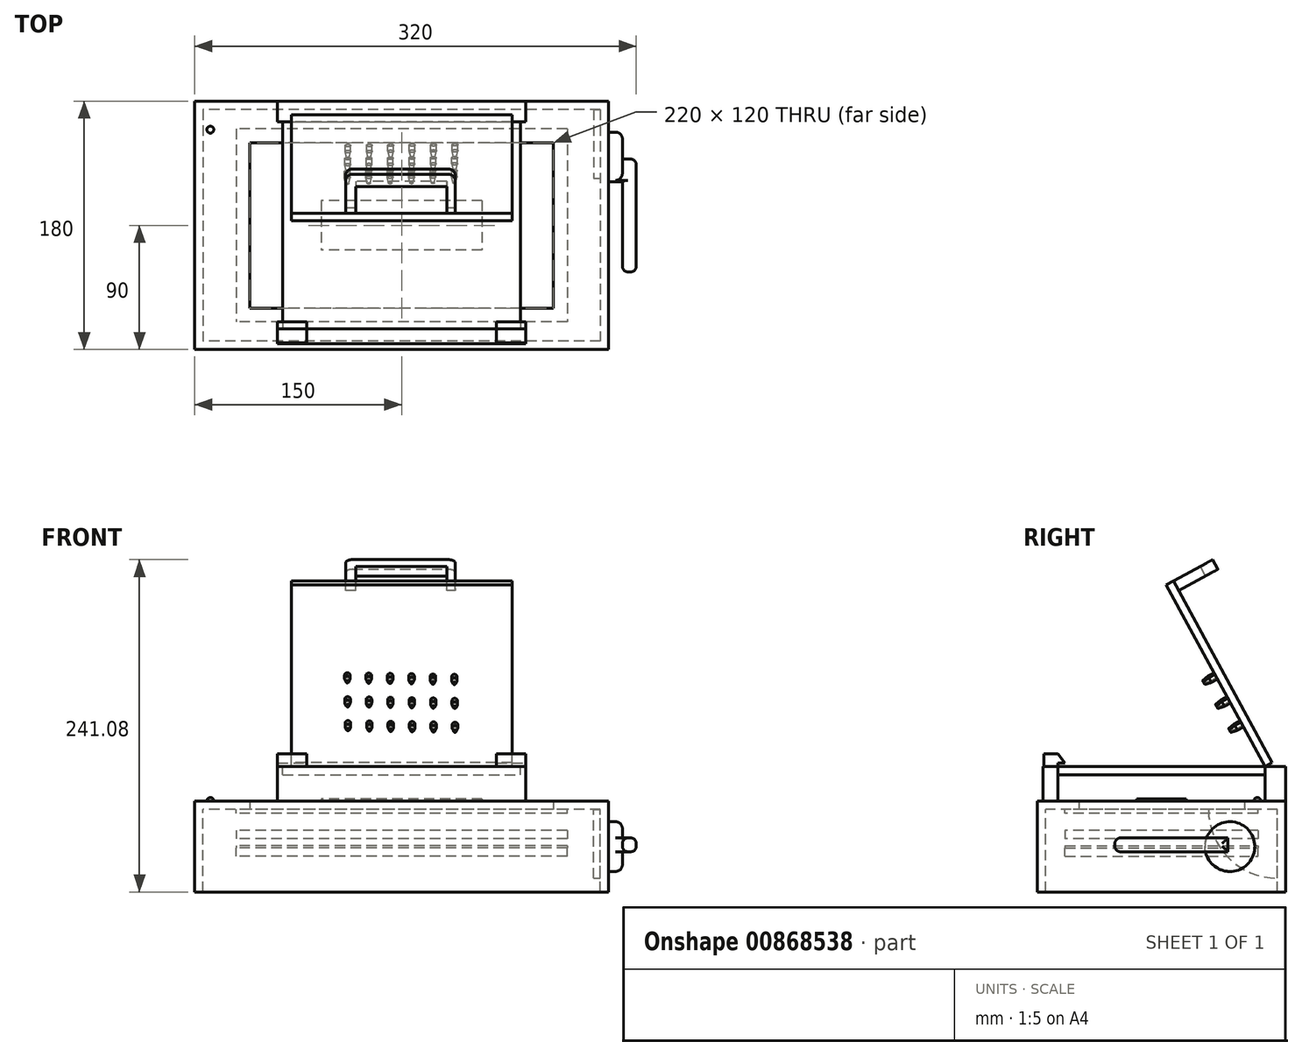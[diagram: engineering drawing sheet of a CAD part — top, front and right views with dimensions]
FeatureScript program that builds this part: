
annotation { "Feature Type Name" : "Feature", "Feature Type Description" : "" }
export const myFeature = defineFeature(function(context is Context, id is Id, definition is map)
    precondition{}
    {
        {
            var Q0;
            Q0=qCreatedBy(makeId("Top.planeOp"),FACE);
            var sketch = newSketch(context, id + "F0", { "sketchPlane" : qUnion([Q0])});
            skLineSegment(sketch, "E0.bottom", {"start": v(150, 90) * mm, "end": v(-150, 90) * mm});
            skLineSegment(sketch, "E0.top", {"start": v(150, -90) * mm, "end": v(-150, -90) * mm});
            skLineSegment(sketch, "E0.left", {"start": v(150, 90) * mm, "end": v(150, -90) * mm});
            skLineSegment(sketch, "E0.right", {"start": v(-150, 90) * mm, "end": v(-150, -90) * mm});
            skPoint(sketch, "E0.middle", {"position": v(0, 0) * mm});
            skLineSegment(sketch, "E1.bottom", {"start": v(110, 60) * mm, "end": v(-110, 60) * mm});
            skLineSegment(sketch, "E1.top", {"start": v(110, -60) * mm, "end": v(-110, -60) * mm});
            skLineSegment(sketch, "E1.left", {"start": v(110, 60) * mm, "end": v(110, -60) * mm});
            skLineSegment(sketch, "E1.right", {"start": v(-110, 60) * mm, "end": v(-110, -60) * mm});
            skSolve(sketch);
        }
        {
            var Q0;
            Q0 = qSketchRegion(id + "F0", true);
            extrude(context, id + "F1", {"entities" : qUnion([Q0]), "depth" : 6 * mm, "offsetDistance" : 25 * mm});
        }
        {
            var Q0;
            Q0=qCreatedBy(makeId("Top.planeOp"),FACE);
            var sketch = newSketch(context, id + "F2", { "sketchPlane" : qUnion([Q0])});
            skLineSegment(sketch, "E2.bottom", {"start": v(120, 70) * mm, "end": v(-120, 70) * mm});
            skLineSegment(sketch, "E2.top", {"start": v(120, -70) * mm, "end": v(-120, -70) * mm});
            skLineSegment(sketch, "E2.left", {"start": v(120, 70) * mm, "end": v(120, -70) * mm});
            skLineSegment(sketch, "E2.right", {"start": v(-120, 70) * mm, "end": v(-120, -70) * mm});
            skPoint(sketch, "E2.middle", {"position": v(0, 0) * mm});
            skSolve(sketch);
        }
        {
            var Q0;
            Q0 = qSketchRegion(id + "F2", true);
            extrude(context, id + "F3", {"entities" : qUnion([Q0]), "oppositeDirection" : true, "depth" : 3 * mm, "offsetDistance" : 25 * mm});
        }
        {
            var Q0;
            Q0=makeQuery(id+"F1.opExtrude","CAP_FACE",FACE,{"disambiguationData":[OSD([sQuery(id+"F0.wireOp",EDGE,"E0.bottom"),sQuery(id+"F0.wireOp",EDGE,"E0.top"),sQuery(id+"F0.wireOp",EDGE,"E0.left"),sQuery(id+"F0.wireOp",EDGE,"E0.right"),sQuery(id+"F0.wireOp",EDGE,"E1.bottom"),sQuery(id+"F0.wireOp",EDGE,"E1.top"),sQuery(id+"F0.wireOp",EDGE,"E1.left"),sQuery(id+"F0.wireOp",EDGE,"E1.right")])],"isStart":true});
            var sketch = newSketch(context, id + "F4", { "sketchPlane" : qUnion([Q0])});
            skLineSegment(sketch, "E3.bottom", {"start": v(144, -84) * mm, "end": v(-144, -84) * mm});
            skLineSegment(sketch, "E3.top", {"start": v(144, 84) * mm, "end": v(-144, 84) * mm});
            skLineSegment(sketch, "E3.left", {"start": v(144, -84) * mm, "end": v(144, 84) * mm});
            skLineSegment(sketch, "E3.right", {"start": v(-144, -84) * mm, "end": v(-144, 84) * mm});
            skPoint(sketch, "E3.middle", {"position": v(0, 0) * mm});
            skLineSegment(sketch, "E4.bottom", {"start": v(-150, 90) * mm, "end": v(150, 90) * mm});
            skLineSegment(sketch, "E4.top", {"start": v(-150, -90) * mm, "end": v(150, -90) * mm});
            skLineSegment(sketch, "E4.left", {"start": v(-150, 90) * mm, "end": v(-150, -90) * mm});
            skLineSegment(sketch, "E4.right", {"start": v(150, 90) * mm, "end": v(150, -90) * mm});
            skSolve(sketch);
        }
        {
            var Q0;
            Q0 = qSketchRegion(id + "F4", true);
            extrude(context, id + "F5", {"entities" : qUnion([Q0]), "operationType" : NewBodyOperationType.ADD, "depth" : 60 * mm, "offsetDistance" : 25 * mm});
        }
        {
            var Q0;
            Q0=makeQuery(id+"F5.opExtrude","SWEPT_FACE",FACE,{"disambiguationData":[OSD([sQuery(id+"F4.wireOp",EDGE,"E3.left")])]});
            var sketch = newSketch(context, id + "F6", { "sketchPlane" : qUnion([Q0])});
            skArc(sketch, "E5", {"start": v(-34, 0) * mm, "mid": v(-48.64, -35.36) * mm, "end": v(-84, -50) * mm});
            skArc(sketch, "E6", {"start": v(-24, 0) * mm, "mid": v(-41.57, -42.43) * mm, "end": v(-84, -60) * mm});
            skSolve(sketch);
        }
        {
            var Q0;
            {var subQ0=sQuery(id+"F6.wireOp",EDGE,"E5");Q0=makeQuery(id+"F6.imprint","IMPRINT",FACE,{"disambiguationData":[TD([[makeQuery(id+"F6.imprint","IMPRINT",EDGE,{"derivedFrom":subQ0}),1.0]])]});}
            extrude(context, id + "F7", {"entities" : qUnion([Q0]), "depth" : 5 * mm, "offsetDistance" : 25 * mm});
        }
        {
            var Q0;
            Q0=makeQuery(id+"F1.opExtrude","CAP_FACE",FACE,{"disambiguationData":[OSD([sQuery(id+"F0.wireOp",EDGE,"E0.bottom"),sQuery(id+"F0.wireOp",EDGE,"E0.top"),sQuery(id+"F0.wireOp",EDGE,"E0.left"),sQuery(id+"F0.wireOp",EDGE,"E0.right"),sQuery(id+"F0.wireOp",EDGE,"E1.bottom"),sQuery(id+"F0.wireOp",EDGE,"E1.top"),sQuery(id+"F0.wireOp",EDGE,"E1.left"),sQuery(id+"F0.wireOp",EDGE,"E1.right")])],"isStart":false});
            var sketch = newSketch(context, id + "F8", { "sketchPlane" : qUnion([Q0])});
            skLineSegment(sketch, "E7.bottom", {"start": v(-90, 90) * mm, "end": v(90, 90) * mm});
            skLineSegment(sketch, "E7.top", {"start": v(-90, 75) * mm, "end": v(90, 75) * mm});
            skLineSegment(sketch, "E7.left", {"start": v(-90, 90) * mm, "end": v(-90, 75) * mm});
            skLineSegment(sketch, "E7.right", {"start": v(90, 90) * mm, "end": v(90, 75) * mm});
            skLineSegment(sketch, "E8.bottom", {"start": v(-90, -75) * mm, "end": v(90, -75) * mm});
            skLineSegment(sketch, "E8.top", {"start": v(-90, -90) * mm, "end": v(90, -90) * mm});
            skLineSegment(sketch, "E8.left", {"start": v(-90, -75) * mm, "end": v(-90, -90) * mm});
            skLineSegment(sketch, "E8.right", {"start": v(90, -75) * mm, "end": v(90, -90) * mm});
            skSolve(sketch);
        }
        {
            var Q0;
            Q0 = qSketchRegion(id + "F8", true);
            extrude(context, id + "F9", {"entities" : qUnion([Q0]), "operationType" : NewBodyOperationType.ADD, "depth" : 25 * mm, "offsetDistance" : 25 * mm});
        }
        {
            var Q0;
            Q0=makeQuery(id+"F9.opExtrude","CAP_FACE",FACE,{"disambiguationData":[OSD([sQuery(id+"F8.wireOp",EDGE,"E7.bottom"),sQuery(id+"F8.wireOp",EDGE,"E7.top"),sQuery(id+"F8.wireOp",EDGE,"E7.left"),sQuery(id+"F8.wireOp",EDGE,"E7.right")])],"isStart":false});
            var sketch = newSketch(context, id + "F10", { "sketchPlane" : qUnion([Q0])});
            skLineSegment(sketch, "E9.bottom", {"start": v(86.22, 75) * mm, "end": v(-86.22, 75) * mm});
            skLineSegment(sketch, "E9.top", {"start": v(86.22, -75) * mm, "end": v(-86.22, -75) * mm});
            skLineSegment(sketch, "E9.left", {"start": v(86.22, 75) * mm, "end": v(86.22, -75) * mm});
            skLineSegment(sketch, "E9.right", {"start": v(-86.22, 75) * mm, "end": v(-86.22, -75) * mm});
            skPoint(sketch, "E9.middle", {"position": v(0, 0) * mm});
            skSolve(sketch);
        }
        {
            var Q0;
            Q0 = qSketchRegion(id + "F10", true);
            extrude(context, id + "F11", {"entities" : qUnion([Q0]), "oppositeDirection" : true, "depth" : 6 * mm, "offsetDistance" : 25 * mm});
        }
        {
            var Q0;
            Q0=makeQuery(id+"F3.opExtrude","CAP_FACE",FACE,{"disambiguationData":[OSD([sQuery(id+"F2.wireOp",EDGE,"E2.bottom"),sQuery(id+"F2.wireOp",EDGE,"E2.top"),sQuery(id+"F2.wireOp",EDGE,"E2.left"),sQuery(id+"F2.wireOp",EDGE,"E2.right")])],"isStart":false});
            cPlane(context, id + "F12", {"entities" : qUnion([Q0]), "cplaneType" : CPlaneType.OFFSET, "offset" : 25 * mm, "width" : 150 * mm, "height" : 150 * mm});
        }
        {
            var Q0;
            Q0=qCreatedBy(id+"F12.planeOp",FACE);
            var sketch = newSketch(context, id + "F13", { "sketchPlane" : qUnion([Q0])});
            skLineSegment(sketch, "E10.bottom", {"start": v(120, 70) * mm, "end": v(-120, 70) * mm});
            skLineSegment(sketch, "E10.top", {"start": v(120, -70) * mm, "end": v(-120, -70) * mm});
            skLineSegment(sketch, "E10.left", {"start": v(120, 70) * mm, "end": v(120, -70) * mm});
            skLineSegment(sketch, "E10.right", {"start": v(-120, 70) * mm, "end": v(-120, -70) * mm});
            skPoint(sketch, "E10.middle", {"position": v(0, 0) * mm});
            skSolve(sketch);
        }
        {
            var Q0;
            Q0=makeQuery(id+"F13.imprint","IMPRINT",FACE,{"disambiguationData":[TD([[makeQuery(id+"F13.imprint","IMPRINT",EDGE,{"derivedFrom":sQuery(id+"F13.wireOp",EDGE,"E10.bottom")}),1.0]])]});
            extrude(context, id + "F14", {"entities" : qUnion([Q0]), "depth" : 6 * mm, "offsetDistance" : 25 * mm});
        }
        {
            var Q0;
            Q0=makeQuery(id+"F14.opExtrude","CAP_FACE",FACE,{"disambiguationData":[OSD([sQuery(id+"F13.wireOp",EDGE,"E10.bottom"),sQuery(id+"F13.wireOp",EDGE,"E10.top"),sQuery(id+"F13.wireOp",EDGE,"E10.left"),sQuery(id+"F13.wireOp",EDGE,"E10.right")])],"isStart":true});
            extrude(context, id + "F15", {"entities" : qUnion([Q0]), "depth" : 1.6 * mm, "offsetDistance" : 25 * mm});
        }
        {
            var Q0;
            Q0=makeQuery(id+"F15.opExtrude","CAP_FACE",FACE,{"disambiguationData":[OSD([sQuery(id+"F13.wireOp",EDGE,"E10.bottom"),sQuery(id+"F13.wireOp",EDGE,"E10.top"),sQuery(id+"F13.wireOp",EDGE,"E10.left"),sQuery(id+"F13.wireOp",EDGE,"E10.right")])],"isStart":false});
            cPlane(context, id + "F16", {"entities" : qUnion([Q0]), "cplaneType" : CPlaneType.OFFSET, "offset" : 5 * mm, "width" : 150 * mm, "height" : 150 * mm});
        }
        {
            var Q0;
            Q0=qCreatedBy(id+"F16.planeOp",FACE);
            var sketch = newSketch(context, id + "F17", { "sketchPlane" : qUnion([Q0])});
            skLineSegment(sketch, "E11.bottom", {"start": v(120, 70) * mm, "end": v(-120, 70) * mm});
            skLineSegment(sketch, "E11.top", {"start": v(120, -70) * mm, "end": v(-120, -70) * mm});
            skLineSegment(sketch, "E11.left", {"start": v(120, 70) * mm, "end": v(120, -70) * mm});
            skLineSegment(sketch, "E11.right", {"start": v(-120, 70) * mm, "end": v(-120, -70) * mm});
            skPoint(sketch, "E11.middle", {"position": v(0, 0) * mm});
            skSolve(sketch);
        }
        {
            var Q0;
            Q0=makeQuery(id+"F17.imprint","IMPRINT",FACE,{"disambiguationData":[TD([[makeQuery(id+"F17.imprint","IMPRINT",EDGE,{"derivedFrom":sQuery(id+"F17.wireOp",EDGE,"E11.bottom")}),1.0]])]});
            extrude(context, id + "F18", {"entities" : qUnion([Q0]), "depth" : 6 * mm, "offsetDistance" : 25 * mm});
        }
        {
            var Q0;
            Q0=qCreatedBy(makeId("Right.planeOp"),FACE);
            var sketch = newSketch(context, id + "F19", { "sketchPlane" : qUnion([Q0])});
            skLineSegment(sketch, "E12.bottom", {"start": v(75, 31) * mm, "end": v(3.46, 162.84) * mm});
            skLineSegment(sketch, "E12.top", {"start": v(80.27, 33.86) * mm, "end": v(8.74, 165.7) * mm});
            skLineSegment(sketch, "E12.left", {"start": v(75, 31) * mm, "end": v(80.27, 33.86) * mm});
            skLineSegment(sketch, "E12.right", {"start": v(3.46, 162.84) * mm, "end": v(8.74, 165.7) * mm});
            skSolve(sketch);
        }
        {
            var Q0;
            Q0=makeQuery(id+"F19.imprint","IMPRINT",FACE,{"disambiguationData":[TD([[makeQuery(id+"F19.imprint","IMPRINT",EDGE,{"derivedFrom":sQuery(id+"F19.wireOp",EDGE,"E12.bottom")}),-1.0]])]});
            extrude(context, id + "F20", {"entities" : qUnion([Q0]), "depth" : 80 * mm, "offsetDistance" : 25 * mm, "hasSecondDirection" : true, "secondDirectionOppositeDirection" : true, "secondDirectionDepth" : 80 * mm});
        }
        {
            var Q0;
            Q0=makeQuery(id+"F20.opExtrude","SWEPT_FACE",FACE,{"disambiguationData":[OSD([sQuery(id+"F19.wireOp",EDGE,"E12.bottom")])]});
            var sketch = newSketch(context, id + "F21", { "sketchPlane" : qUnion([Q0])});
            skCircle(sketch, "E13", {"center": v(-39.43, 66.88) * mm, "radius": 2 * mm});
            skCircle(sketch, "E14.0.1.0", {"center": v(-39.2, 47.12) * mm, "radius": 2 * mm});
            skCircle(sketch, "E14.0.2.0", {"center": v(-38.98, 27.36) * mm, "radius": 2 * mm});
            skCircle(sketch, "E14.1.0.0", {"center": v(-23.9, 66.62) * mm, "radius": 2 * mm});
            skCircle(sketch, "E14.1.1.0", {"center": v(-23.68, 46.86) * mm, "radius": 2 * mm});
            skCircle(sketch, "E14.1.2.0", {"center": v(-23.46, 27.1) * mm, "radius": 2 * mm});
            skCircle(sketch, "E14.2.0.0", {"center": v(-8.38, 66.36) * mm, "radius": 2 * mm});
            skCircle(sketch, "E14.2.1.0", {"center": v(-8.16, 46.6) * mm, "radius": 2 * mm});
            skCircle(sketch, "E14.2.2.0", {"center": v(-7.94, 26.84) * mm, "radius": 2 * mm});
            skCircle(sketch, "E14.3.0.0", {"center": v(7.14, 66.1) * mm, "radius": 2 * mm});
            skCircle(sketch, "E14.3.1.0", {"center": v(7.36, 46.34) * mm, "radius": 2 * mm});
            skCircle(sketch, "E14.3.2.0", {"center": v(7.58, 26.59) * mm, "radius": 2 * mm});
            skCircle(sketch, "E14.4.0.0", {"center": v(22.66, 65.84) * mm, "radius": 2 * mm});
            skCircle(sketch, "E14.4.1.0", {"center": v(22.88, 46.09) * mm, "radius": 2 * mm});
            skCircle(sketch, "E14.4.2.0", {"center": v(23.1, 26.33) * mm, "radius": 2 * mm});
            skCircle(sketch, "E14.5.0.0", {"center": v(38.18, 65.59) * mm, "radius": 2 * mm});
            skCircle(sketch, "E14.5.1.0", {"center": v(38.4, 45.83) * mm, "radius": 2 * mm});
            skCircle(sketch, "E14.5.2.0", {"center": v(38.63, 26.07) * mm, "radius": 2 * mm});
            skLineSegment(sketch, "E14.direction1", {"start": v(-39.43, 66.88) * mm, "end": v(-23.9, 66.62) * mm, "construction": true});
            skLineSegment(sketch, "E14.direction2", {"start": v(-39.43, 66.88) * mm, "end": v(-39.2, 47.12) * mm, "construction": true});
            skSolve(sketch);
        }
        {
            var Q0;
            Q0 = qSketchRegion(id + "F21", true);
            extrude(context, id + "F22", {"entities" : qUnion([Q0]), "operationType" : NewBodyOperationType.ADD, "depth" : 10 * mm, "offsetDistance" : 25 * mm});
        }
        {
            var Q0;
            Q0=makeQuery(id+"F5.boolean.opBoolean","MERGE",FACE,{"derivedFrom":[makeQuery(id+"F1.opExtrude","SWEPT_FACE",FACE,{"disambiguationData":[OSD([sQuery(id+"F0.wireOp",EDGE,"E0.left")])]}),makeQuery(id+"F5.opExtrude","SWEPT_FACE",FACE,{"disambiguationData":[OSD([sQuery(id+"F4.wireOp",EDGE,"E4.right")])]})]});
            var sketch = newSketch(context, id + "F23", { "sketchPlane" : qUnion([Q0])});
            skCircle(sketch, "E15", {"center": v(49.56, -27.08) * mm, "radius": 18.06 * mm});
            skSolve(sketch);
        }
        {
            var Q0;
            Q0=makeQuery(id+"F23.imprint","IMPRINT",FACE,{"disambiguationData":[TD([[makeQuery(id+"F23.imprint","IMPRINT",EDGE,{"derivedFrom":sQuery(id+"F23.wireOp",EDGE,"E15")}),1.0]])]});
            extrude(context, id + "F24", {"entities" : qUnion([Q0]), "operationType" : NewBodyOperationType.ADD, "depth" : 10 * mm, "offsetDistance" : 25 * mm});
        }
        {
            var Q0;
            Q0=makeQuery(id+"F24.opExtrude","CAP_FACE",FACE,{"disambiguationData":[OSD([sQuery(id+"F23.wireOp",EDGE,"E15")])],"isStart":false});
            var sketch = newSketch(context, id + "F25", { "sketchPlane" : qUnion([Q0])});
            skLineSegment(sketch, "E16.bottom", {"start": v(48.06, -20.82) * mm, "end": v(-33.79, -20.82) * mm});
            skLineSegment(sketch, "E16.top", {"start": v(48.06, -30.84) * mm, "end": v(-33.79, -30.84) * mm});
            skLineSegment(sketch, "E16.left", {"start": v(48.06, -20.82) * mm, "end": v(48.06, -30.84) * mm});
            skLineSegment(sketch, "E16.right", {"start": v(-33.79, -20.82) * mm, "end": v(-33.79, -30.84) * mm});
            skSolve(sketch);
        }
        {
            var Q0;
            {var subQ0=sQuery(id+"F25.wireOp",EDGE,"E16.right");Q0=makeQuery(id+"F25.imprint","IMPRINT",FACE,{"disambiguationData":[TD([[makeQuery(id+"F25.imprint","IMPRINT",EDGE,{"derivedFrom":subQ0}),1.0]])]});}
            var Q1;
            {var subQ0=sQuery(id+"F25.wireOp",EDGE,"E16.left");Q1=makeQuery(id+"F25.imprint","IMPRINT",FACE,{"disambiguationData":[TD([[makeQuery(id+"F25.imprint","IMPRINT",EDGE,{"derivedFrom":subQ0}),-1.0]])]});}
            extrude(context, id + "F26", {"entities" : qUnion([Q0, Q1]), "operationType" : NewBodyOperationType.ADD, "depth" : 10 * mm, "offsetDistance" : 25 * mm});
        }
        {
            var Q0;
            Q0=makeQuery(id+"F26.opExtrude","CAP_EDGE",EDGE,{"disambiguationData":[OSD([sQuery(id+"F25.wireOp",EDGE,"E16.bottom")])],"isStart":false});
            var Q1;
            {var subQ0=sQuery(id+"F25.wireOp",EDGE,"E16.bottom");Q1=makeQuery(id+"F26.boolean.opBoolean","SPLIT",EDGE,{"disambiguationData":[topologyDisambiguationEdgeConnected([makeQuery(id+"F26.opExtrude","CAP_FACE",FACE,{"disambiguationData":[OSD([subQ0,sQuery(id+"F25.wireOp",EDGE,"E16.top"),sQuery(id+"F25.wireOp",EDGE,"E16.left"),sQuery(id+"F25.wireOp",EDGE,"E16.right")])],"isStart":true})])],"derivedFrom":makeQuery(id+"F26.opExtrude","CAP_EDGE",EDGE,{"disambiguationData":[OSD([subQ0])],"isStart":true})});}
            var Q2;
            Q2=makeQuery(id+"F26.opExtrude","CAP_EDGE",EDGE,{"disambiguationData":[OSD([sQuery(id+"F25.wireOp",EDGE,"E16.top")])],"isStart":false});
            var Q3;
            {var subQ0=sQuery(id+"F25.wireOp",EDGE,"E16.top");Q3=makeQuery(id+"F26.boolean.opBoolean","SPLIT",EDGE,{"disambiguationData":[topologyDisambiguationEdgeConnected([makeQuery(id+"F26.opExtrude","CAP_FACE",FACE,{"disambiguationData":[OSD([sQuery(id+"F25.wireOp",EDGE,"E16.bottom"),subQ0,sQuery(id+"F25.wireOp",EDGE,"E16.left"),sQuery(id+"F25.wireOp",EDGE,"E16.right")])],"isStart":true})])],"derivedFrom":makeQuery(id+"F26.opExtrude","CAP_EDGE",EDGE,{"disambiguationData":[OSD([subQ0])],"isStart":true})});}
            var Q4;
            Q4=makeQuery(id+"F26.opExtrude","SWEPT_FACE",FACE,{"disambiguationData":[OSD([sQuery(id+"F25.wireOp",EDGE,"E16.right")])]});
            var Q5;
            Q5=makeQuery(id+"F26.opExtrude","CAP_EDGE",EDGE,{"disambiguationData":[OSD([sQuery(id+"F25.wireOp",EDGE,"E16.left")])],"isStart":false});
            fillet(context, id + "F27", {"entities" : qUnion([Q0, Q1, Q2, Q3, Q4, Q5]), "radius" : 4 * mm, "tangentPropagation" : true, "allowEdgeOverflow" : false});
        }
        {
            var Q0;
            Q0=makeQuery(id+"F9.opExtrude","SWEPT_FACE",FACE,{"disambiguationData":[OSD([sQuery(id+"F8.wireOp",EDGE,"E8.right")])]});
            var sketch = newSketch(context, id + "F28", { "sketchPlane" : qUnion([Q0])});
            skLineSegment(sketch, "E17.bottom", {"start": v(-85.35, 40.17) * mm, "end": v(-75, 40.17) * mm});
            skLineSegment(sketch, "E17.top", {"start": v(-85.35, 31) * mm, "end": v(-75, 31) * mm});
            skLineSegment(sketch, "E17.left", {"start": v(-85.35, 40.17) * mm, "end": v(-85.35, 31) * mm});
            skLineSegment(sketch, "E18", {"start": v(-75, 40.17) * mm, "end": v(-69.91, 33.67) * mm});
            skLineSegment(sketch, "E19", {"start": v(-69.91, 33.67) * mm, "end": v(-75, 33.67) * mm});
            skLineSegment(sketch, "E20", {"start": v(-75, 33.67) * mm, "end": v(-75, 31) * mm});
            skSolve(sketch);
        }
        {
            var Q0;
            Q0=makeQuery(id+"F28.imprint","IMPRINT",FACE,{"disambiguationData":[TD([[makeQuery(id+"F28.imprint","IMPRINT",EDGE,{"derivedFrom":sQuery(id+"F28.wireOp",EDGE,"E17.bottom")}),-1.0]])]});
            var Q1;
            Q1=sQuery(id+"F28.wireOp",EDGE,"E19");
            var Q2;
            Q2=sQuery(id+"F28.wireOp",EDGE,"E18");
            var Q3;
            Q3=sQuery(id+"F28.wireOp",EDGE,"E17.bottom");
            var Q4;
            Q4=sQuery(id+"F28.wireOp",EDGE,"E17.left");
            var Q5;
            Q5=makeQuery(id+"F9.opExtrude","SWEPT_FACE",FACE,{"disambiguationData":[OSD([sQuery(id+"F8.wireOp",EDGE,"E8.left")])]});
            extrude(context, id + "F29", {"entities" : qUnion([Q0]), "surfaceEntities" : qUnion([Q1, Q2, Q3, Q4]), "endBound" : BoundingType.UP_TO_SURFACE, "oppositeDirection" : true, "depth" : 25 * mm, "endBoundEntityFace" : qUnion([Q5]), "offsetDistance" : 25 * mm});
        }
        {
            var Q0;
            Q0=makeQuery(id+"F29.opExtrude","SWEPT_FACE",FACE,{"disambiguationData":[OSD([sQuery(id+"F28.wireOp",EDGE,"E17.left")])]});
            var sketch = newSketch(context, id + "F30", { "sketchPlane" : qUnion([Q0])});
            skLineSegment(sketch, "E21.bottom", {"start": v(-68.72, 40.17) * mm, "end": v(68.82, 40.17) * mm});
            skLineSegment(sketch, "E21.top", {"start": v(-68.72, 31) * mm, "end": v(68.82, 31) * mm});
            skLineSegment(sketch, "E21.left", {"start": v(-68.72, 40.17) * mm, "end": v(-68.72, 31) * mm});
            skLineSegment(sketch, "E21.right", {"start": v(68.82, 40.17) * mm, "end": v(68.82, 31) * mm});
            skSolve(sketch);
        }
        {
            var Q0;
            Q0=makeQuery(id+"F30.imprint","IMPRINT",FACE,{"disambiguationData":[TD([[makeQuery(id+"F30.imprint","IMPRINT",EDGE,{"derivedFrom":sQuery(id+"F30.wireOp",EDGE,"E21.bottom")}),-1.0]])]});
            extrude(context, id + "F31", {"entities" : qUnion([Q0]), "operationType" : NewBodyOperationType.REMOVE, "oppositeDirection" : true, "depth" : 25 * mm, "offsetDistance" : 25 * mm});
        }
        {
            var Q0;
            Q0=makeQuery(id+"F20.opExtrude","SWEPT_FACE",FACE,{"disambiguationData":[OSD([sQuery(id+"F19.wireOp",EDGE,"E12.right")])]});
            var sketch = newSketch(context, id + "F32", { "sketchPlane" : qUnion([Q0])});
            skLineSegment(sketch, "E22", {"start": v(-40.61, 86.7) * mm, "end": v(-40.61, 118.94) * mm});
            skLineSegment(sketch, "E23", {"start": v(-40.61, 118.94) * mm, "end": v(38.75, 118.94) * mm});
            skLineSegment(sketch, "E24", {"start": v(38.75, 118.94) * mm, "end": v(38.75, 86.7) * mm});
            skLineSegment(sketch, "E25", {"start": v(38.75, 86.7) * mm, "end": v(32.75, 86.7) * mm});
            skLineSegment(sketch, "E26", {"start": v(32.75, 86.7) * mm, "end": v(32.75, 108.67) * mm});
            skLineSegment(sketch, "E27", {"start": v(32.75, 108.67) * mm, "end": v(-33.38, 108.67) * mm});
            skLineSegment(sketch, "E28", {"start": v(-33.38, 108.67) * mm, "end": v(-33.38, 86.7) * mm});
            skLineSegment(sketch, "E29", {"start": v(-33.38, 86.7) * mm, "end": v(-40.61, 86.7) * mm});
            skSolve(sketch);
        }
        {
            var Q0;
            Q0=makeQuery(id+"F32.imprint","IMPRINT",FACE,{"disambiguationData":[TD([[makeQuery(id+"F32.imprint","IMPRINT",EDGE,{"derivedFrom":sQuery(id+"F32.wireOp",EDGE,"E22")}),-1.0]])]});
            extrude(context, id + "F33", {"entities" : qUnion([Q0]), "oppositeDirection" : true, "depth" : 8 * mm, "offsetDistance" : 25 * mm});
        }
        {
            var Q0;
            Q0=makeQuery(id+"F33.opExtrude","SWEPT_EDGE",EDGE,{"disambiguationData":[OSD([sQuery(id+"F32.wireOp",EDGE,"E22"),sQuery(id+"F32.wireOp",EDGE,"E23")])]});
            var Q1;
            Q1=makeQuery(id+"F33.opExtrude","SWEPT_EDGE",EDGE,{"disambiguationData":[OSD([sQuery(id+"F32.wireOp",EDGE,"E23"),sQuery(id+"F32.wireOp",EDGE,"E24")])]});
            fillet(context, id + "F34", {"entities" : qUnion([Q0, Q1]), "radius" : 5 * mm, "tangentPropagation" : true, "allowEdgeOverflow" : false});
        }
        {
            var Q0;
            Q0=makeQuery(id+"F1.opExtrude","CAP_FACE",FACE,{"disambiguationData":[OSD([sQuery(id+"F0.wireOp",EDGE,"E0.bottom"),sQuery(id+"F0.wireOp",EDGE,"E0.top"),sQuery(id+"F0.wireOp",EDGE,"E0.left"),sQuery(id+"F0.wireOp",EDGE,"E0.right"),sQuery(id+"F0.wireOp",EDGE,"E1.bottom"),sQuery(id+"F0.wireOp",EDGE,"E1.top"),sQuery(id+"F0.wireOp",EDGE,"E1.left"),sQuery(id+"F0.wireOp",EDGE,"E1.right")])],"isStart":false});
            var sketch = newSketch(context, id + "F35", { "sketchPlane" : qUnion([Q0])});
            skLineSegment(sketch, "E30.bottom", {"start": v(58.23, 17.98) * mm, "end": v(-58.23, 17.98) * mm});
            skLineSegment(sketch, "E30.top", {"start": v(58.23, -17.98) * mm, "end": v(-58.23, -17.98) * mm});
            skLineSegment(sketch, "E30.left", {"start": v(58.23, 17.98) * mm, "end": v(58.23, -17.98) * mm});
            skLineSegment(sketch, "E30.right", {"start": v(-58.23, 17.98) * mm, "end": v(-58.23, -17.98) * mm});
            skPoint(sketch, "E30.middle", {"position": v(0, 0) * mm});
            skSolve(sketch);
        }
        {
            var Q0;
            Q0=makeQuery(id+"F35.imprint","IMPRINT",FACE,{"disambiguationData":[TD([[makeQuery(id+"F35.imprint","IMPRINT",EDGE,{"derivedFrom":sQuery(id+"F35.wireOp",EDGE,"E30.bottom")}),1.0]])]});
            extrude(context, id + "F36", {"entities" : qUnion([Q0]), "depth" : 1.6 * mm, "offsetDistance" : 25 * mm});
        }
        {
            var Q0;
            Q0=makeQuery(id+"F9.boolean.opBoolean","MERGE",FACE,{"derivedFrom":[makeQuery(id+"F5.boolean.opBoolean","MERGE",FACE,{"derivedFrom":[makeQuery(id+"F1.opExtrude","SWEPT_FACE",FACE,{"disambiguationData":[OSD([sQuery(id+"F0.wireOp",EDGE,"E0.top")])]}),makeQuery(id+"F5.opExtrude","SWEPT_FACE",FACE,{"disambiguationData":[OSD([sQuery(id+"F4.wireOp",EDGE,"E4.bottom")])]})]}),makeQuery(id+"F9.opExtrude","SWEPT_FACE",FACE,{"disambiguationData":[OSD([sQuery(id+"F8.wireOp",EDGE,"E8.top")])]})]});
            var sketch = newSketch(context, id + "F37", { "sketchPlane" : qUnion([Q0])});
            skLineSegment(sketch, "E31.bottom", {"start": v(120, 6) * mm, "end": v(-120, 6) * mm});
            skLineSegment(sketch, "E31.top", {"start": v(120, 56) * mm, "end": v(-120, 56) * mm});
            skLineSegment(sketch, "E31.left", {"start": v(120, 6) * mm, "end": v(120, 56) * mm});
            skLineSegment(sketch, "E31.right", {"start": v(-120, 6) * mm, "end": v(-120, 56) * mm});
            skPoint(sketch, "E31.middle", {"position": v(0, 31) * mm});
            skSolve(sketch);
        }
        {
            var Q0;
            Q0=makeQuery(id+"F37.imprint","IMPRINT",FACE,{"disambiguationData":[TD([[makeQuery(id+"F37.imprint","IMPRINT",EDGE,{"derivedFrom":sQuery(id+"F37.wireOp",EDGE,"E31.top")}),1.0]])]});
            var Q1;
            {var subQ1=sQuery(id+"F8.wireOp",EDGE,"E8.top");Q1=makeQuery(id+"F37.imprint","IMPRINT",FACE,{"disambiguationData":[TD([[makeQuery(id+"F37.imprint","IMPRINT",EDGE,{"derivedFrom":makeQuery(id+"F9.opExtrude","CAP_EDGE",EDGE,{"disambiguationData":[OSD([subQ1])],"isStart":false})}),1.0]])]});}
            extrude(context, id + "F38", {"entities" : qUnion([Q0, Q1]), "operationType" : NewBodyOperationType.REMOVE, "oppositeDirection" : true, "depth" : 4 * mm, "offsetDistance" : 25 * mm});
        }
        {
            var Q0;
            {var subQ0=sQuery(id+"F23.wireOp",EDGE,"E15");Q0=makeQuery(id+"F26.boolean.opBoolean","SPLIT",EDGE,{"disambiguationData":[topologyDisambiguationEdgeConnected([makeQuery(id+"F24.opExtrude","CAP_FACE",FACE,{"disambiguationData":[OSD([subQ0])],"isStart":false})])],"derivedFrom":makeQuery(id+"F24.opExtrude","CAP_EDGE",EDGE,{"disambiguationData":[OSD([subQ0])],"isStart":false})});}
            fillet(context, id + "F39", {"entities" : qUnion([Q0]), "radius" : 5 * mm, "tangentPropagation" : true, "allowEdgeOverflow" : false});
        }
        {
            var Q0;
            Q0=makeQuery(id+"F22.opExtrude","CAP_FACE",FACE,{"disambiguationData":[OSD([sQuery(id+"F21.wireOp",EDGE,"E14.2.0.0")])],"isStart":false});
            var Q1;
            Q1=makeQuery(id+"F22.opExtrude","CAP_FACE",FACE,{"disambiguationData":[OSD([sQuery(id+"F21.wireOp",EDGE,"E14.1.0.0")])],"isStart":false});
            var Q2;
            Q2=makeQuery(id+"F22.opExtrude","CAP_FACE",FACE,{"disambiguationData":[OSD([sQuery(id+"F21.wireOp",EDGE,"E14.4.0.0")])],"isStart":false});
            var Q3;
            Q3=makeQuery(id+"F22.opExtrude","CAP_FACE",FACE,{"disambiguationData":[OSD([sQuery(id+"F21.wireOp",EDGE,"E14.3.0.0")])],"isStart":false});
            var Q4;
            Q4=makeQuery(id+"F22.opExtrude","CAP_FACE",FACE,{"disambiguationData":[OSD([sQuery(id+"F21.wireOp",EDGE,"E14.5.0.0")])],"isStart":false});
            var Q5;
            Q5=makeQuery(id+"F22.opExtrude","CAP_FACE",FACE,{"disambiguationData":[OSD([sQuery(id+"F21.wireOp",EDGE,"E13")])],"isStart":false});
            var Q6;
            Q6=makeQuery(id+"F22.opExtrude","CAP_EDGE",EDGE,{"disambiguationData":[OSD([sQuery(id+"F21.wireOp",EDGE,"E14.2.0.0")])],"isStart":false});
            var Q7;
            Q7=makeQuery(id+"F22.opExtrude","CAP_EDGE",EDGE,{"disambiguationData":[OSD([sQuery(id+"F21.wireOp",EDGE,"E14.4.0.0")])],"isStart":false});
            var Q8;
            Q8=makeQuery(id+"F22.opExtrude","CAP_EDGE",EDGE,{"disambiguationData":[OSD([sQuery(id+"F21.wireOp",EDGE,"E13")])],"isStart":false});
            var Q9;
            Q9=makeQuery(id+"F22.opExtrude","CAP_EDGE",EDGE,{"disambiguationData":[OSD([sQuery(id+"F21.wireOp",EDGE,"E14.3.0.0")])],"isStart":false});
            var Q10;
            Q10=makeQuery(id+"F22.opExtrude","CAP_EDGE",EDGE,{"disambiguationData":[OSD([sQuery(id+"F21.wireOp",EDGE,"E14.1.0.0")])],"isStart":false});
            var Q11;
            Q11=makeQuery(id+"F22.opExtrude","CAP_EDGE",EDGE,{"disambiguationData":[OSD([sQuery(id+"F21.wireOp",EDGE,"E14.5.0.0")])],"isStart":false});
            var Q12;
            Q12=makeQuery(id+"F22.opExtrude","CAP_FACE",FACE,{"disambiguationData":[OSD([sQuery(id+"F21.wireOp",EDGE,"E14.1.1.0")])],"isStart":false});
            var Q13;
            Q13=makeQuery(id+"F22.opExtrude","CAP_FACE",FACE,{"disambiguationData":[OSD([sQuery(id+"F21.wireOp",EDGE,"E14.2.1.0")])],"isStart":false});
            var Q14;
            Q14=makeQuery(id+"F22.opExtrude","CAP_FACE",FACE,{"disambiguationData":[OSD([sQuery(id+"F21.wireOp",EDGE,"E14.4.1.0")])],"isStart":false});
            var Q15;
            Q15=makeQuery(id+"F22.opExtrude","CAP_FACE",FACE,{"disambiguationData":[OSD([sQuery(id+"F21.wireOp",EDGE,"E14.3.1.0")])],"isStart":false});
            var Q16;
            Q16=makeQuery(id+"F22.opExtrude","CAP_FACE",FACE,{"disambiguationData":[OSD([sQuery(id+"F21.wireOp",EDGE,"E14.0.1.0")])],"isStart":false});
            var Q17;
            Q17=makeQuery(id+"F22.opExtrude","CAP_FACE",FACE,{"disambiguationData":[OSD([sQuery(id+"F21.wireOp",EDGE,"E14.5.1.0")])],"isStart":false});
            var Q18;
            Q18=makeQuery(id+"F22.opExtrude","CAP_EDGE",EDGE,{"disambiguationData":[OSD([sQuery(id+"F21.wireOp",EDGE,"E14.4.1.0")])],"isStart":false});
            var Q19;
            Q19=makeQuery(id+"F22.opExtrude","CAP_EDGE",EDGE,{"disambiguationData":[OSD([sQuery(id+"F21.wireOp",EDGE,"E14.1.1.0")])],"isStart":false});
            var Q20;
            Q20=makeQuery(id+"F22.opExtrude","CAP_EDGE",EDGE,{"disambiguationData":[OSD([sQuery(id+"F21.wireOp",EDGE,"E14.3.1.0")])],"isStart":false});
            var Q21;
            Q21=makeQuery(id+"F22.opExtrude","CAP_EDGE",EDGE,{"disambiguationData":[OSD([sQuery(id+"F21.wireOp",EDGE,"E14.2.1.0")])],"isStart":false});
            var Q22;
            Q22=makeQuery(id+"F22.opExtrude","CAP_EDGE",EDGE,{"disambiguationData":[OSD([sQuery(id+"F21.wireOp",EDGE,"E14.0.1.0")])],"isStart":false});
            var Q23;
            Q23=makeQuery(id+"F22.opExtrude","CAP_EDGE",EDGE,{"disambiguationData":[OSD([sQuery(id+"F21.wireOp",EDGE,"E14.5.1.0")])],"isStart":false});
            var Q24;
            Q24=makeQuery(id+"F22.opExtrude","CAP_FACE",FACE,{"disambiguationData":[OSD([sQuery(id+"F21.wireOp",EDGE,"E14.4.2.0")])],"isStart":false});
            var Q25;
            Q25=makeQuery(id+"F22.opExtrude","CAP_FACE",FACE,{"disambiguationData":[OSD([sQuery(id+"F21.wireOp",EDGE,"E14.0.2.0")])],"isStart":false});
            var Q26;
            Q26=makeQuery(id+"F22.opExtrude","CAP_FACE",FACE,{"disambiguationData":[OSD([sQuery(id+"F21.wireOp",EDGE,"E14.1.2.0")])],"isStart":false});
            var Q27;
            Q27=makeQuery(id+"F22.opExtrude","CAP_FACE",FACE,{"disambiguationData":[OSD([sQuery(id+"F21.wireOp",EDGE,"E14.5.2.0")])],"isStart":false});
            var Q28;
            Q28=makeQuery(id+"F22.opExtrude","CAP_FACE",FACE,{"disambiguationData":[OSD([sQuery(id+"F21.wireOp",EDGE,"E14.3.2.0")])],"isStart":false});
            var Q29;
            Q29=makeQuery(id+"F22.opExtrude","CAP_FACE",FACE,{"disambiguationData":[OSD([sQuery(id+"F21.wireOp",EDGE,"E14.2.2.0")])],"isStart":false});
            var Q30;
            Q30=makeQuery(id+"F22.opExtrude","CAP_EDGE",EDGE,{"disambiguationData":[OSD([sQuery(id+"F21.wireOp",EDGE,"E14.3.2.0")])],"isStart":false});
            var Q31;
            Q31=makeQuery(id+"F22.opExtrude","CAP_EDGE",EDGE,{"disambiguationData":[OSD([sQuery(id+"F21.wireOp",EDGE,"E14.0.2.0")])],"isStart":false});
            var Q32;
            Q32=makeQuery(id+"F22.opExtrude","CAP_EDGE",EDGE,{"disambiguationData":[OSD([sQuery(id+"F21.wireOp",EDGE,"E14.1.2.0")])],"isStart":false});
            var Q33;
            Q33=makeQuery(id+"F22.opExtrude","CAP_EDGE",EDGE,{"disambiguationData":[OSD([sQuery(id+"F21.wireOp",EDGE,"E14.2.2.0")])],"isStart":false});
            var Q34;
            Q34=makeQuery(id+"F22.opExtrude","CAP_EDGE",EDGE,{"disambiguationData":[OSD([sQuery(id+"F21.wireOp",EDGE,"E14.5.2.0")])],"isStart":false});
            var Q35;
            Q35=makeQuery(id+"F22.opExtrude","CAP_EDGE",EDGE,{"disambiguationData":[OSD([sQuery(id+"F21.wireOp",EDGE,"E14.4.2.0")])],"isStart":false});
            chamfer(context, id + "F40", {"entities" : qUnion([Q0, Q1, Q2, Q3, Q4, Q5, Q6, Q7, Q8, Q9, Q10, Q11, Q12, Q13, Q14, Q15, Q16, Q17, Q18, Q19, Q20, Q21, Q22, Q23, Q24, Q25, Q26, Q27, Q28, Q29, Q30, Q31, Q32, Q33, Q34, Q35]), "chamferType" : ChamferType.TWO_OFFSETS, "width1" : 1 * mm, "oppositeDirection" : false, "width2" : 5 * mm, "tangentPropagation" : true});
        }
        {
            var Q0;
            Q0=makeQuery(id+"F38.boolean.opBoolean","MERGE",FACE,{"derivedFrom":[makeQuery(id+"F1.opExtrude","CAP_FACE",FACE,{"disambiguationData":[OSD([sQuery(id+"F0.wireOp",EDGE,"E0.bottom"),sQuery(id+"F0.wireOp",EDGE,"E0.top"),sQuery(id+"F0.wireOp",EDGE,"E0.left"),sQuery(id+"F0.wireOp",EDGE,"E0.right"),sQuery(id+"F0.wireOp",EDGE,"E1.bottom"),sQuery(id+"F0.wireOp",EDGE,"E1.top"),sQuery(id+"F0.wireOp",EDGE,"E1.left"),sQuery(id+"F0.wireOp",EDGE,"E1.right")])],"isStart":false})],"fromTools":[makeQuery(id+"F38.opExtrude","SWEPT_FACE",FACE,{"disambiguationData":[OSD([sQuery(id+"F37.wireOp",EDGE,"E31.bottom")])]})]});
            var sketch = newSketch(context, id + "F41", { "sketchPlane" : qUnion([Q0])});
            skCircle(sketch, "E32", {"center": v(-138.68, 69.42) * mm, "radius": 2.5 * mm});
            skSolve(sketch);
        }
        {
            var Q0;
            Q0=makeQuery(id+"F41.imprint","IMPRINT",FACE,{"disambiguationData":[TD([[makeQuery(id+"F41.imprint","IMPRINT",EDGE,{"derivedFrom":sQuery(id+"F41.wireOp",EDGE,"E32")}),1.0]])]});
            extrude(context, id + "F42", {"entities" : qUnion([Q0]), "depth" : 2.5 * mm, "offsetDistance" : 25 * mm});
        }
        {
            var Q0;
            Q0=makeQuery(id+"F42.opExtrude","CAP_EDGE",EDGE,{"disambiguationData":[OSD([sQuery(id+"F41.wireOp",EDGE,"E32")])],"isStart":false});
            fillet(context, id + "F43", {"entities" : qUnion([Q0]), "radius" : 2.5 * mm, "tangentPropagation" : true, "allowEdgeOverflow" : false});
        }
    });
